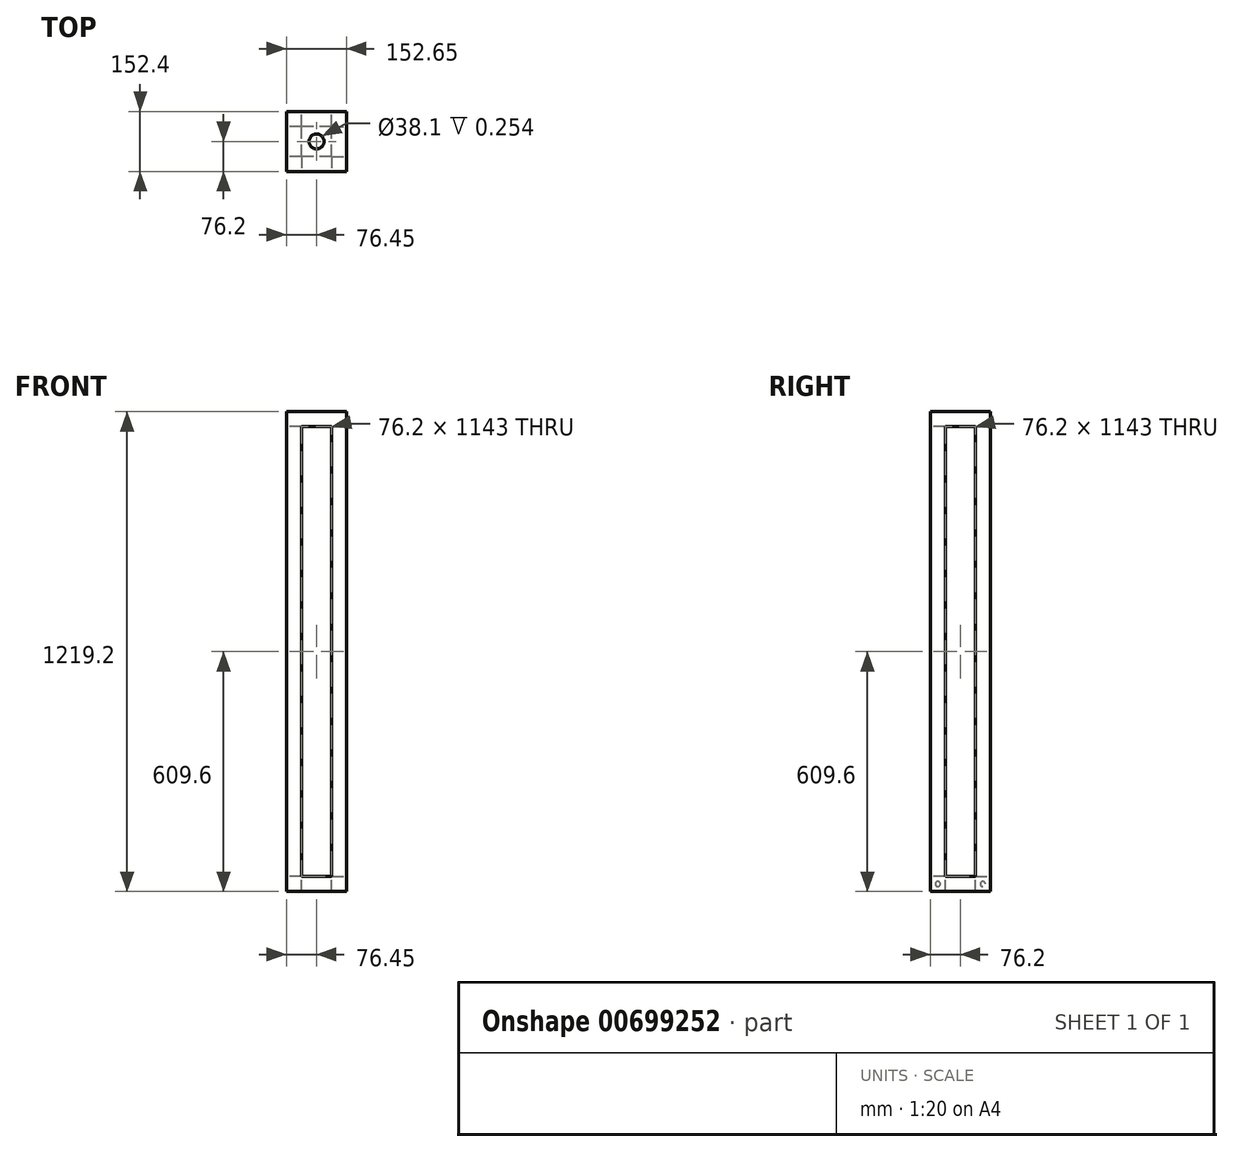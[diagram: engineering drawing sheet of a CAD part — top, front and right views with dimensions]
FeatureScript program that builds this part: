
annotation { "Feature Type Name" : "Feature", "Feature Type Description" : "" }
export const myFeature = defineFeature(function(context is Context, id is Id, definition is map)
    precondition{}
    {
        {
            var Q0;
            Q0=qCreatedBy(makeId("Top.planeOp"),FACE);
            var sketch = newSketch(context, id + "F0", { "sketchPlane" : qUnion([Q0])});
            skLineSegment(sketch, "E0.bottom", {"start": v(76.2, -76.2) * mm, "end": v(-76.2, -76.2) * mm});
            skLineSegment(sketch, "E0.top", {"start": v(76.2, 76.2) * mm, "end": v(-76.2, 76.2) * mm});
            skLineSegment(sketch, "E0.left", {"start": v(76.2, -76.2) * mm, "end": v(76.2, 76.2) * mm});
            skLineSegment(sketch, "E0.right", {"start": v(-76.2, -76.2) * mm, "end": v(-76.2, 76.2) * mm});
            skPoint(sketch, "E0.middle", {"position": v(0, 0) * mm});
            skSolve(sketch);
        }
        {
            var Q0;
            Q0 = qSketchRegion(id + "F0", true);
            extrude(context, id + "F1", {"entities" : qUnion([Q0]), "oppositeDirection" : true, "depth" : 38.1 * mm, "offsetDistance" : 25.4 * mm});
        }
        {
            var Q0;
            Q0=makeQuery(id+"F1.opExtrude","CAP_FACE",FACE,{"disambiguationData":[OSD([sQuery(id+"F0.wireOp",EDGE,"E0.bottom"),sQuery(id+"F0.wireOp",EDGE,"E0.top"),sQuery(id+"F0.wireOp",EDGE,"E0.left"),sQuery(id+"F0.wireOp",EDGE,"E0.right")])],"isStart":true});
            var sketch = newSketch(context, id + "F2", { "sketchPlane" : qUnion([Q0])});
            skLineSegment(sketch, "E1.bottom", {"start": v(38.1, -38.1) * mm, "end": v(-38.1, -38.1) * mm});
            skLineSegment(sketch, "E1.top", {"start": v(38.1, 38.1) * mm, "end": v(-38.1, 38.1) * mm});
            skLineSegment(sketch, "E1.left", {"start": v(38.1, -38.1) * mm, "end": v(38.1, 38.1) * mm});
            skLineSegment(sketch, "E1.right", {"start": v(-38.1, -38.1) * mm, "end": v(-38.1, 38.1) * mm});
            skPoint(sketch, "E1.middle", {"position": v(0, 0) * mm});
            skSolve(sketch);
        }
        {
            var Q0;
            Q0 = qSketchRegion(id + "F2", true);
            extrude(context, id + "F3", {"entities" : qUnion([Q0]), "operationType" : NewBodyOperationType.REMOVE, "oppositeDirection" : true, "depth" : 38.1 * mm, "offsetDistance" : 25.4 * mm});
        }
        {
            var Q0;
            Q0=makeQuery(id+"F1.opExtrude","CAP_FACE",FACE,{"disambiguationData":[OSD([sQuery(id+"F0.wireOp",EDGE,"E0.bottom"),sQuery(id+"F0.wireOp",EDGE,"E0.top"),sQuery(id+"F0.wireOp",EDGE,"E0.left"),sQuery(id+"F0.wireOp",EDGE,"E0.right")])],"isStart":true});
            var sketch = newSketch(context, id + "F4", { "sketchPlane" : qUnion([Q0])});
            skLineSegment(sketch, "E2.bottom", {"start": v(-38.1, -38.1) * mm, "end": v(-76.2, -38.1) * mm});
            skLineSegment(sketch, "E2.top", {"start": v(-38.1, -76.2) * mm, "end": v(-76.2, -76.2) * mm});
            skLineSegment(sketch, "E2.left", {"start": v(-38.1, -38.1) * mm, "end": v(-38.1, -76.2) * mm});
            skLineSegment(sketch, "E2.right", {"start": v(-76.2, -38.1) * mm, "end": v(-76.2, -76.2) * mm});
            skLineSegment(sketch, "E3.bottom", {"start": v(-38.1, 38.1) * mm, "end": v(-76.2, 38.1) * mm});
            skLineSegment(sketch, "E3.top", {"start": v(-38.1, 76.2) * mm, "end": v(-76.2, 76.2) * mm});
            skLineSegment(sketch, "E3.left", {"start": v(-38.1, 38.1) * mm, "end": v(-38.1, 76.2) * mm});
            skLineSegment(sketch, "E3.right", {"start": v(-76.2, 38.1) * mm, "end": v(-76.2, 76.2) * mm});
            skLineSegment(sketch, "E4.bottom", {"start": v(38.1, 38.1) * mm, "end": v(76.2, 38.1) * mm});
            skLineSegment(sketch, "E4.top", {"start": v(38.1, 76.2) * mm, "end": v(76.2, 76.2) * mm});
            skLineSegment(sketch, "E4.left", {"start": v(38.1, 38.1) * mm, "end": v(38.1, 76.2) * mm});
            skLineSegment(sketch, "E4.right", {"start": v(76.2, 38.1) * mm, "end": v(76.2, 76.2) * mm});
            skLineSegment(sketch, "E5.bottom", {"start": v(38.1, -38.1) * mm, "end": v(76.2, -38.1) * mm});
            skLineSegment(sketch, "E5.top", {"start": v(38.1, -76.2) * mm, "end": v(76.2, -76.2) * mm});
            skLineSegment(sketch, "E5.left", {"start": v(38.1, -38.1) * mm, "end": v(38.1, -76.2) * mm});
            skLineSegment(sketch, "E5.right", {"start": v(76.2, -38.1) * mm, "end": v(76.2, -76.2) * mm});
            skSolve(sketch);
        }
        {
            var Q0;
            Q0 = qSketchRegion(id + "F4", true);
            extrude(context, id + "F5", {"entities" : qUnion([Q0]), "operationType" : NewBodyOperationType.ADD, "depth" : 1143 * mm, "offsetDistance" : 25.4 * mm});
        }
        {
            var Q0;
            Q0=makeQuery(id+"F5.opExtrude","CAP_FACE",FACE,{"disambiguationData":[OSD([sQuery(id+"F4.wireOp",EDGE,"E3.bottom"),sQuery(id+"F4.wireOp",EDGE,"E3.top"),sQuery(id+"F4.wireOp",EDGE,"E3.left"),sQuery(id+"F4.wireOp",EDGE,"E3.right")])],"isStart":false});
            var sketch = newSketch(context, id + "F6", { "sketchPlane" : qUnion([Q0])});
            skLineSegment(sketch, "E6.bottom", {"start": v(-76.2, 76.2) * mm, "end": v(76.2, 76.2) * mm});
            skLineSegment(sketch, "E6.top", {"start": v(-76.2, -76.2) * mm, "end": v(76.2, -76.2) * mm});
            skLineSegment(sketch, "E6.left", {"start": v(-76.2, 76.2) * mm, "end": v(-76.2, -76.2) * mm});
            skLineSegment(sketch, "E6.right", {"start": v(76.2, 76.2) * mm, "end": v(76.2, -76.2) * mm});
            skSolve(sketch);
        }
        {
            var Q0;
            Q0 = qSketchRegion(id + "F6", true);
            extrude(context, id + "F7", {"entities" : qUnion([Q0]), "operationType" : NewBodyOperationType.ADD, "depth" : 38.1 * mm, "offsetDistance" : 25.4 * mm});
        }
        {
            var Q0;
            Q0=makeQuery(id+"F7.boolean.opBoolean","MERGE",FACE,{"derivedFrom":[makeQuery(id+"F5.boolean.opBoolean","MERGE",FACE,{"derivedFrom":[makeQuery(id+"F1.opExtrude","SWEPT_FACE",FACE,{"disambiguationData":[OSD([sQuery(id+"F0.wireOp",EDGE,"E0.right")])]}),makeQuery(id+"F5.opExtrude","SWEPT_FACE",FACE,{"disambiguationData":[OSD([sQuery(id+"F4.wireOp",EDGE,"E2.right")])]}),makeQuery(id+"F5.opExtrude","SWEPT_FACE",FACE,{"disambiguationData":[OSD([sQuery(id+"F4.wireOp",EDGE,"E3.right")])]})]}),makeQuery(id+"F7.opExtrude","SWEPT_FACE",FACE,{"disambiguationData":[OSD([sQuery(id+"F6.wireOp",EDGE,"E6.left")])]})]});
            var sketch = newSketch(context, id + "F8", { "sketchPlane" : qUnion([Q0])});
            skLineSegment(sketch, "E7.bottom", {"start": v(-38.1, 0) * mm, "end": v(-76.2, 0) * mm});
            skLineSegment(sketch, "E7.top", {"start": v(-38.1, -38.1) * mm, "end": v(-76.2, -38.1) * mm});
            skLineSegment(sketch, "E7.left", {"start": v(-38.1, 0) * mm, "end": v(-38.1, -38.1) * mm});
            skLineSegment(sketch, "E7.right", {"start": v(-76.2, 0) * mm, "end": v(-76.2, -38.1) * mm});
            skLineSegment(sketch, "E8.bottom", {"start": v(38.1, 0) * mm, "end": v(76.2, 0) * mm});
            skLineSegment(sketch, "E8.top", {"start": v(38.1, -38.1) * mm, "end": v(76.2, -38.1) * mm});
            skLineSegment(sketch, "E8.left", {"start": v(38.1, 0) * mm, "end": v(38.1, -38.1) * mm});
            skLineSegment(sketch, "E8.right", {"start": v(76.2, 0) * mm, "end": v(76.2, -38.1) * mm});
            skCircle(sketch, "E9", {"center": v(-57.15, -19.05) * mm, "radius": 6.35 * mm});
            skPoint(sketch, "E9.centerSnap0", {"position": v(-38.1, -19.05) * mm});
            skPoint(sketch, "E9.centerSnap1", {"position": v(-57.15, 0) * mm});
            skCircle(sketch, "E10", {"center": v(57.15, -19.05) * mm, "radius": 6.35 * mm});
            skPoint(sketch, "E10.centerSnap0", {"position": v(76.2, -19.05) * mm});
            skPoint(sketch, "E10.centerSnap1", {"position": v(57.15, 0) * mm});
            skSolve(sketch);
        }
        {
            var Q0;
            Q0=makeQuery(id+"F8.imprint","IMPRINT",FACE,{"disambiguationData":[TD([[makeQuery(id+"F8.imprint","IMPRINT",EDGE,{"derivedFrom":sQuery(id+"F8.wireOp",EDGE,"E9")}),1.0]])]});
            var Q1;
            Q1=makeQuery(id+"F8.imprint","IMPRINT",FACE,{"disambiguationData":[TD([[makeQuery(id+"F8.imprint","IMPRINT",EDGE,{"derivedFrom":sQuery(id+"F8.wireOp",EDGE,"E10")}),1.0]])]});
            extrude(context, id + "F9", {"entities" : qUnion([Q0, Q1]), "operationType" : NewBodyOperationType.ADD, "depth" : 0.25 * mm, "offsetDistance" : 25.4 * mm});
        }
        {
            var Q0;
            Q0=makeQuery(id+"F7.opExtrude","CAP_FACE",FACE,{"disambiguationData":[OSD([sQuery(id+"F6.wireOp",EDGE,"E6.bottom"),sQuery(id+"F6.wireOp",EDGE,"E6.top"),sQuery(id+"F6.wireOp",EDGE,"E6.left"),sQuery(id+"F6.wireOp",EDGE,"E6.right")])],"isStart":false});
            var sketch = newSketch(context, id + "F10", { "sketchPlane" : qUnion([Q0])});
            skCircle(sketch, "E11", {"center": v(0, 0) * mm, "radius": 19.05 * mm});
            skSolve(sketch);
        }
        {
            var Q0;
            Q0 = qSketchRegion(id + "F10", true);
            extrude(context, id + "F11", {"entities" : qUnion([Q0]), "operationType" : NewBodyOperationType.REMOVE, "oppositeDirection" : true, "depth" : 0.25 * mm, "offsetDistance" : 25.4 * mm});
        }
    });
